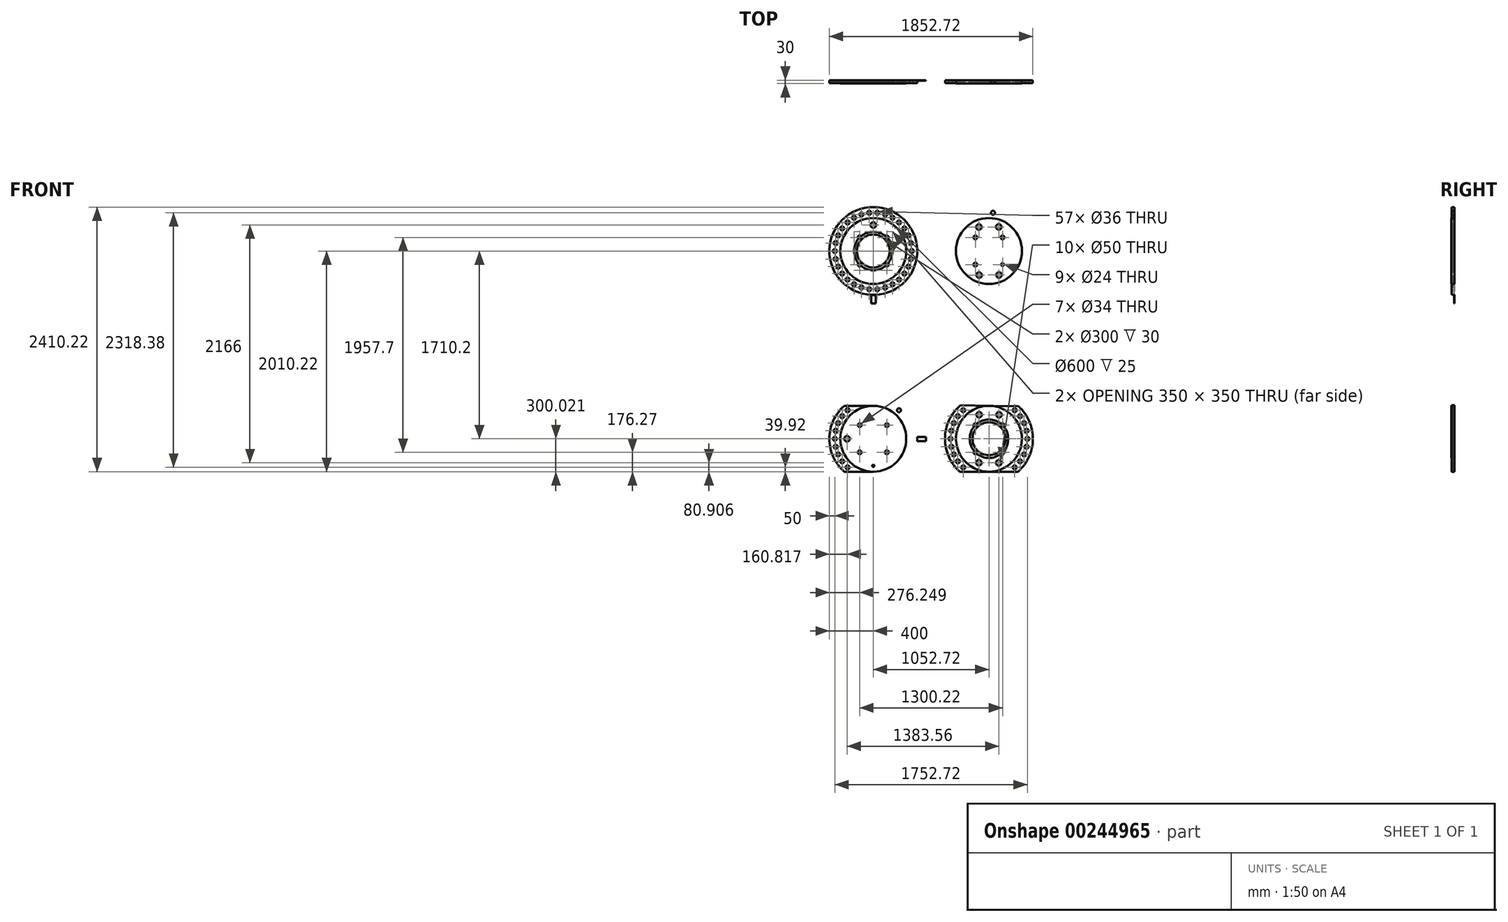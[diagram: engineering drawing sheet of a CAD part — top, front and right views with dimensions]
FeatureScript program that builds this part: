
annotation { "Feature Type Name" : "Feature", "Feature Type Description" : "" }
export const myFeature = defineFeature(function(context is Context, id is Id, definition is map)
    precondition{}
    {
        {
            var Q0;
            Q0=qCreatedBy(makeId("Front.planeOp"),FACE);
            var sketch = newSketch(context, id + "F0", { "sketchPlane" : qUnion([Q0])});
            skCircle(sketch, "E0", {"center": v(0, 0) * mm, "radius": 150 * mm});
            skCircle(sketch, "E1", {"center": v(0, 0) * mm, "radius": 175 * mm});
            skLineSegment(sketch, "E2", {"start": v(-223.66, 0) * mm, "end": v(241.08, 0) * mm, "construction": true});
            skCircle(sketch, "E3", {"center": v(-123.75, 123.74) * mm, "radius": 12 * mm});
            skCircle(sketch, "E4.1.0", {"center": v(-123.74, -123.75) * mm, "radius": 12 * mm});
            skCircle(sketch, "E4.2.0", {"center": v(123.75, -123.74) * mm, "radius": 12 * mm});
            skCircle(sketch, "E4.3.0", {"center": v(123.74, 123.75) * mm, "radius": 12 * mm});
            skLineSegment(sketch, "E5", {"start": v(0, 0) * mm, "end": v(0, 220.77) * mm, "construction": true});
            skCircle(sketch, "E6", {"center": v(-123.75, 123.74) * mm, "radius": 17 * mm});
            skCircle(sketch, "E7", {"center": v(123.74, 123.75) * mm, "radius": 17 * mm});
            skCircle(sketch, "E8", {"center": v(123.75, -123.74) * mm, "radius": 17 * mm});
            skCircle(sketch, "E9", {"center": v(-123.74, -123.75) * mm, "radius": 17 * mm});
            skCircle(sketch, "E10", {"center": v(0, 0) * mm, "radius": 300 * mm});
            skCircle(sketch, "E11", {"center": v(0, 0) * mm, "radius": 350 * mm, "construction": true});
            skCircle(sketch, "E12", {"center": v(0, 0) * mm, "radius": 400 * mm});
            skCircle(sketch, "E13", {"center": v(-350, 0) * mm, "radius": 18 * mm});
            skCircle(sketch, "E14.1.0", {"center": v(-342.35, -72.77) * mm, "radius": 18 * mm});
            skCircle(sketch, "E14.2.0", {"center": v(-319.74, -142.36) * mm, "radius": 18 * mm});
            skCircle(sketch, "E14.3.0", {"center": v(-283.16, -205.72) * mm, "radius": 18 * mm});
            skCircle(sketch, "E14.4.0", {"center": v(-234.2, -260.1) * mm, "radius": 18 * mm});
            skCircle(sketch, "E14.5.0", {"center": v(-175, -303.1) * mm, "radius": 18 * mm});
            skCircle(sketch, "E14.6.0", {"center": v(-108.16, -332.87) * mm, "radius": 18 * mm});
            skCircle(sketch, "E14.7.0", {"center": v(-36.58, -348.08) * mm, "radius": 18 * mm});
            skCircle(sketch, "E14.8.0", {"center": v(36.58, -348.08) * mm, "radius": 18 * mm});
            skCircle(sketch, "E14.9.0", {"center": v(108.16, -332.87) * mm, "radius": 18 * mm});
            skCircle(sketch, "E14.10.0", {"center": v(175, -303.1) * mm, "radius": 18 * mm});
            skCircle(sketch, "E14.11.0", {"center": v(234.2, -260.1) * mm, "radius": 18 * mm});
            skCircle(sketch, "E14.12.0", {"center": v(283.16, -205.72) * mm, "radius": 18 * mm});
            skCircle(sketch, "E14.13.0", {"center": v(319.74, -142.36) * mm, "radius": 18 * mm});
            skCircle(sketch, "E14.14.0", {"center": v(342.35, -72.77) * mm, "radius": 18 * mm});
            skCircle(sketch, "E14.15.0", {"center": v(350, 0) * mm, "radius": 18 * mm});
            skCircle(sketch, "E14.16.0", {"center": v(342.35, 72.77) * mm, "radius": 18 * mm});
            skCircle(sketch, "E14.17.0", {"center": v(319.74, 142.36) * mm, "radius": 18 * mm});
            skCircle(sketch, "E14.18.0", {"center": v(283.16, 205.72) * mm, "radius": 18 * mm});
            skCircle(sketch, "E14.19.0", {"center": v(234.2, 260.1) * mm, "radius": 18 * mm});
            skCircle(sketch, "E14.20.0", {"center": v(175, 303.1) * mm, "radius": 18 * mm});
            skCircle(sketch, "E14.21.0", {"center": v(108.16, 332.87) * mm, "radius": 18 * mm});
            skCircle(sketch, "E14.22.0", {"center": v(36.58, 348.08) * mm, "radius": 18 * mm});
            skCircle(sketch, "E14.23.0", {"center": v(-36.58, 348.08) * mm, "radius": 18 * mm});
            skCircle(sketch, "E14.24.0", {"center": v(-108.16, 332.87) * mm, "radius": 18 * mm});
            skCircle(sketch, "E14.25.0", {"center": v(-175, 303.1) * mm, "radius": 18 * mm});
            skCircle(sketch, "E14.26.0", {"center": v(-234.2, 260.1) * mm, "radius": 18 * mm});
            skCircle(sketch, "E14.27.0", {"center": v(-283.16, 205.72) * mm, "radius": 18 * mm});
            skCircle(sketch, "E14.28.0", {"center": v(-319.74, 142.36) * mm, "radius": 18 * mm});
            skCircle(sketch, "E14.29.0", {"center": v(-342.35, 72.77) * mm, "radius": 18 * mm});
            skLineSegment(sketch, "E15", {"start": v(526.36, 521.4) * mm, "end": v(526.36, -601.38) * mm});
            skPoint(sketch, "E16.center", {"position": v(0, 9.08) * mm});
            skPoint(sketch, "E17.MirrorP", {"position": v(1052.72, 0) * mm});
            skPoint(sketch, "E18.MirrorP", {"position": v(1052.72, 9.08) * mm});
            skCircle(sketch, "E19.MirrorC", {"center": v(928.98, 123.75) * mm, "radius": 12 * mm});
            skCircle(sketch, "E20.MirrorC", {"center": v(1176.47, 123.74) * mm, "radius": 12 * mm});
            skCircle(sketch, "E21.MirrorC", {"center": v(1089.3, 348.08) * mm, "radius": 18 * mm});
            skCircle(sketch, "E22.MirrorC", {"center": v(1335.88, -205.72) * mm, "radius": 18 * mm});
            skCircle(sketch, "E23.MirrorC", {"center": v(769.56, 205.72) * mm, "radius": 18 * mm});
            skCircle(sketch, "E24.MirrorC", {"center": v(1142.22, 219.11) * mm, "radius": 25 * mm});
            skCircle(sketch, "E25.MirrorC", {"center": v(963.22, -219.11) * mm, "radius": 25 * mm});
            skCircle(sketch, "E26.MirrorC", {"center": v(1286.92, -260.1) * mm, "radius": 18 * mm});
            skCircle(sketch, "E27.MirrorC", {"center": v(1395.07, 72.77) * mm, "radius": 18 * mm});
            skCircle(sketch, "E28.MirrorC", {"center": v(961.07, 218.22) * mm, "radius": 25 * mm});
            skCircle(sketch, "E29.MirrorC", {"center": v(818.53, 260.1) * mm, "radius": 18 * mm});
            skCircle(sketch, "E30.MirrorC", {"center": v(928.97, -123.74) * mm, "radius": 17 * mm});
            skCircle(sketch, "E31.MirrorC", {"center": v(928.98, 123.75) * mm, "radius": 17 * mm});
            skCircle(sketch, "E32.MirrorC", {"center": v(1176.47, 123.74) * mm, "radius": 17 * mm});
            skLineSegment(sketch, "E33.MirrorCS", {"start": v(1276.38, 0) * mm, "end": v(811.64, 0) * mm, "construction": true});
            skCircle(sketch, "E34.MirrorC", {"center": v(1052.72, 0) * mm, "radius": 175 * mm});
            skCircle(sketch, "E35.MirrorC", {"center": v(1052.72, 0) * mm, "radius": 400 * mm});
            skCircle(sketch, "E36.MirrorC", {"center": v(1372.46, -142.36) * mm, "radius": 18 * mm});
            skCircle(sketch, "E37.MirrorC", {"center": v(710.37, 72.77) * mm, "radius": 18 * mm});
            skCircle(sketch, "E38.MirrorC", {"center": v(702.72, 0) * mm, "radius": 18 * mm});
            skCircle(sketch, "E39.MirrorC", {"center": v(1052.72, 0) * mm, "radius": 236.69 * mm, "construction": true});
            skCircle(sketch, "E40.MirrorC", {"center": v(1016.14, 348.08) * mm, "radius": 18 * mm});
            skCircle(sketch, "E41.MirrorC", {"center": v(1227.72, 303.1) * mm, "radius": 18 * mm});
            skCircle(sketch, "E42.MirrorC", {"center": v(732.98, -142.36) * mm, "radius": 18 * mm});
            skCircle(sketch, "E43.MirrorC", {"center": v(818.53, -260.1) * mm, "radius": 18 * mm});
            skCircle(sketch, "E44.MirrorC", {"center": v(1402.72, 0) * mm, "radius": 18 * mm});
            skCircle(sketch, "E45.MirrorC", {"center": v(1395.07, -72.77) * mm, "radius": 18 * mm});
            skCircle(sketch, "E46.MirrorC", {"center": v(1052.72, 0) * mm, "radius": 150 * mm});
            skCircle(sketch, "E47.MirrorC", {"center": v(1286.92, 260.1) * mm, "radius": 18 * mm});
            skCircle(sketch, "E48.MirrorC", {"center": v(1144.37, -218.22) * mm, "radius": 25 * mm});
            skCircle(sketch, "E49.MirrorC", {"center": v(877.72, 303.1) * mm, "radius": 18 * mm});
            skCircle(sketch, "E50.MirrorC", {"center": v(732.98, 142.36) * mm, "radius": 18 * mm});
            skLineSegment(sketch, "E51.MirrorCS", {"start": v(1052.72, 0) * mm, "end": v(1052.72, 220.77) * mm, "construction": true});
            skCircle(sketch, "E52.MirrorC", {"center": v(1052.72, 0) * mm, "radius": 350 * mm, "construction": true});
            skCircle(sketch, "E53.MirrorC", {"center": v(1335.88, 205.72) * mm, "radius": 18 * mm});
            skCircle(sketch, "E54.MirrorC", {"center": v(1160.88, 332.87) * mm, "radius": 18 * mm});
            skCircle(sketch, "E55.MirrorC", {"center": v(1372.46, 142.36) * mm, "radius": 18 * mm});
            skCircle(sketch, "E56.MirrorC", {"center": v(944.56, 332.87) * mm, "radius": 18 * mm});
            skCircle(sketch, "E57.MirrorC", {"center": v(1176.46, -123.75) * mm, "radius": 12 * mm});
            skCircle(sketch, "E58.MirrorC", {"center": v(769.56, -205.72) * mm, "radius": 18 * mm});
            skCircle(sketch, "E59.MirrorC", {"center": v(1052.72, 0) * mm, "radius": 300 * mm});
            skCircle(sketch, "E60.MirrorC", {"center": v(710.37, -72.77) * mm, "radius": 18 * mm});
            skCircle(sketch, "E61.MirrorC", {"center": v(928.97, -123.74) * mm, "radius": 12 * mm});
            skCircle(sketch, "E62.MirrorC", {"center": v(1176.46, -123.75) * mm, "radius": 17 * mm});
            skLineSegment(sketch, "E63", {"start": v(-563.71, -855.1) * mm, "end": v(1645.53, -855.1) * mm});
            skCircle(sketch, "E64.MirrorC", {"center": v(1176.47, -1833.94) * mm, "radius": 17 * mm});
            skCircle(sketch, "E65.MirrorC", {"center": v(928.97, -1586.46) * mm, "radius": 17 * mm});
            skCircle(sketch, "E66.MirrorC", {"center": v(-123.75, -1833.94) * mm, "radius": 12 * mm});
            skPoint(sketch, "E67.MirrorP", {"position": v(1052.72, -1710.2) * mm});
            skPoint(sketch, "E68.MirrorP", {"position": v(0, -1719.28) * mm});
            skCircle(sketch, "E69.MirrorC", {"center": v(1176.46, -1586.45) * mm, "radius": 17 * mm});
            skCircle(sketch, "E70.MirrorC", {"center": v(-123.74, -1586.45) * mm, "radius": 17 * mm});
            skCircle(sketch, "E71.MirrorC", {"center": v(123.75, -1586.46) * mm, "radius": 12 * mm});
            skCircle(sketch, "E72.MirrorC", {"center": v(-123.74, -1586.45) * mm, "radius": 12 * mm});
            skCircle(sketch, "E73.MirrorC", {"center": v(-123.75, -1833.94) * mm, "radius": 17 * mm});
            skCircle(sketch, "E74.MirrorC", {"center": v(928.97, -1586.46) * mm, "radius": 12 * mm});
            skCircle(sketch, "E75.MirrorC", {"center": v(928.98, -1833.95) * mm, "radius": 17 * mm});
            skCircle(sketch, "E76.MirrorC", {"center": v(123.74, -1833.95) * mm, "radius": 12 * mm});
            skCircle(sketch, "E77.MirrorC", {"center": v(928.98, -1833.95) * mm, "radius": 12 * mm});
            skCircle(sketch, "E78.MirrorC", {"center": v(1176.47, -1833.94) * mm, "radius": 12 * mm});
            skCircle(sketch, "E79.MirrorC", {"center": v(1176.46, -1586.45) * mm, "radius": 12 * mm});
            skCircle(sketch, "E80.MirrorC", {"center": v(-319.74, -1567.84) * mm, "radius": 18 * mm});
            skCircle(sketch, "E81.MirrorC", {"center": v(-350, -1710.2) * mm, "radius": 18 * mm});
            skCircle(sketch, "E82.MirrorC", {"center": v(-342.35, -1637.43) * mm, "radius": 18 * mm});
            skCircle(sketch, "E83.MirrorC", {"center": v(-342.35, -1782.97) * mm, "radius": 18 * mm});
            skCircle(sketch, "E84.MirrorC", {"center": v(-319.74, -1852.56) * mm, "radius": 18 * mm});
            skPoint(sketch, "E85.MirrorP", {"position": v(0, -1710.2) * mm});
            skPoint(sketch, "E86.MirrorP", {"position": v(1052.72, -1719.28) * mm});
            skCircle(sketch, "E87.MirrorC", {"center": v(710.37, -1637.43) * mm, "radius": 18 * mm});
            skCircle(sketch, "E88.MirrorC", {"center": v(-283.16, -1915.92) * mm, "radius": 18 * mm});
            skCircle(sketch, "E89.MirrorC", {"center": v(234.2, -1450.1) * mm, "radius": 18 * mm});
            skCircle(sketch, "E90.MirrorC", {"center": v(1052.72, -1710.2) * mm, "radius": 236.69 * mm, "construction": true});
            skCircle(sketch, "E91.MirrorC", {"center": v(-234.2, -1450.1) * mm, "radius": 18 * mm});
            skCircle(sketch, "E92.MirrorC", {"center": v(1052.72, -1710.2) * mm, "radius": 150 * mm});
            skLineSegment(sketch, "E93.MirrorCS", {"start": v(1276.38, -1710.2) * mm, "end": v(811.64, -1710.2) * mm, "construction": true});
            skCircle(sketch, "E94.MirrorC", {"center": v(963.22, -1491.08) * mm, "radius": 25 * mm});
            skCircle(sketch, "E95.MirrorC", {"center": v(-234.2, -1970.3) * mm, "radius": 18 * mm});
            skCircle(sketch, "E96.MirrorC", {"center": v(-283.16, -1504.47) * mm, "radius": 18 * mm});
            skCircle(sketch, "E97.MirrorC", {"center": v(702.72, -1710.2) * mm, "radius": 18 * mm});
            skCircle(sketch, "E98.MirrorC", {"center": v(0, -1710.2) * mm, "radius": 300 * mm});
            skCircle(sketch, "E99.MirrorC", {"center": v(1052.72, -1710.2) * mm, "radius": 350 * mm, "construction": true});
            skCircle(sketch, "E100.MirrorC", {"center": v(123.74, -1833.95) * mm, "radius": 17 * mm});
            skCircle(sketch, "E101.MirrorC", {"center": v(0, -1710.2) * mm, "radius": 400 * mm});
            skCircle(sketch, "E102.MirrorC", {"center": v(1395.07, -1637.43) * mm, "radius": 18 * mm});
            skCircle(sketch, "E103.MirrorC", {"center": v(283.16, -1915.92) * mm, "radius": 18 * mm});
            skCircle(sketch, "E104.MirrorC", {"center": v(319.74, -1852.56) * mm, "radius": 18 * mm});
            skCircle(sketch, "E105.MirrorC", {"center": v(818.53, -1970.3) * mm, "radius": 18 * mm});
            skCircle(sketch, "E106.MirrorC", {"center": v(1052.72, -1710.2) * mm, "radius": 400 * mm});
            skCircle(sketch, "E107.MirrorC", {"center": v(732.98, -1567.84) * mm, "radius": 18 * mm});
            skLineSegment(sketch, "E108.MirrorCS", {"start": v(-223.66, -1710.2) * mm, "end": v(241.08, -1710.2) * mm, "construction": true});
            skCircle(sketch, "E109.MirrorC", {"center": v(769.56, -1504.47) * mm, "radius": 18 * mm});
            skCircle(sketch, "E110.MirrorC", {"center": v(0, -1710.2) * mm, "radius": 175 * mm});
            skCircle(sketch, "E111.MirrorC", {"center": v(769.56, -1915.92) * mm, "radius": 18 * mm});
            skCircle(sketch, "E112.MirrorC", {"center": v(350, -1710.2) * mm, "radius": 18 * mm});
            skCircle(sketch, "E113.MirrorC", {"center": v(961.07, -1928.42) * mm, "radius": 25 * mm});
            skCircle(sketch, "E114.MirrorC", {"center": v(1052.72, -1710.2) * mm, "radius": 175 * mm});
            skCircle(sketch, "E115.MirrorC", {"center": v(1144.37, -1491.98) * mm, "radius": 25 * mm});
            skCircle(sketch, "E116.MirrorC", {"center": v(319.74, -1567.84) * mm, "radius": 18 * mm});
            skCircle(sketch, "E117.MirrorC", {"center": v(1335.88, -1504.47) * mm, "radius": 18 * mm});
            skCircle(sketch, "E118.MirrorC", {"center": v(1372.46, -1852.56) * mm, "radius": 18 * mm});
            skCircle(sketch, "E119.MirrorC", {"center": v(342.35, -1637.43) * mm, "radius": 18 * mm});
            skCircle(sketch, "E120.MirrorC", {"center": v(123.75, -1586.46) * mm, "radius": 17 * mm});
            skCircle(sketch, "E121.MirrorC", {"center": v(1335.88, -1915.92) * mm, "radius": 18 * mm});
            skCircle(sketch, "E122.MirrorC", {"center": v(283.16, -1504.47) * mm, "radius": 18 * mm});
            skCircle(sketch, "E123.MirrorC", {"center": v(1286.92, -1450.1) * mm, "radius": 18 * mm});
            skCircle(sketch, "E124.MirrorC", {"center": v(1052.72, -1710.2) * mm, "radius": 300 * mm});
            skCircle(sketch, "E125.MirrorC", {"center": v(0, -1710.2) * mm, "radius": 350 * mm, "construction": true});
            skCircle(sketch, "E126.MirrorC", {"center": v(234.2, -1970.3) * mm, "radius": 18 * mm});
            skCircle(sketch, "E127.MirrorC", {"center": v(342.35, -1782.97) * mm, "radius": 18 * mm});
            skCircle(sketch, "E128.MirrorC", {"center": v(1372.46, -1567.84) * mm, "radius": 18 * mm});
            skCircle(sketch, "E129.MirrorC", {"center": v(732.98, -1852.56) * mm, "radius": 18 * mm});
            skCircle(sketch, "E130.MirrorC", {"center": v(1286.92, -1970.3) * mm, "radius": 18 * mm});
            skCircle(sketch, "E131.MirrorC", {"center": v(0, -1710.2) * mm, "radius": 150 * mm});
            skCircle(sketch, "E132.MirrorC", {"center": v(1395.07, -1782.97) * mm, "radius": 18 * mm});
            skLineSegment(sketch, "E133.MirrorCS", {"start": v(526.36, -2231.6) * mm, "end": v(526.36, -1108.82) * mm});
            skCircle(sketch, "E134.MirrorC", {"center": v(1402.72, -1710.2) * mm, "radius": 18 * mm});
            skLineSegment(sketch, "E135.MirrorCS", {"start": v(0, -1710.2) * mm, "end": v(0, -1930.97) * mm, "construction": true});
            skLineSegment(sketch, "E136.MirrorCS", {"start": v(1052.72, -1710.2) * mm, "end": v(1052.72, -1930.97) * mm, "construction": true});
            skCircle(sketch, "E137.MirrorC", {"center": v(710.37, -1782.97) * mm, "radius": 18 * mm});
            skCircle(sketch, "E138.MirrorC", {"center": v(818.53, -1450.1) * mm, "radius": 18 * mm});
            skCircle(sketch, "E139.MirrorC", {"center": v(1142.22, -1929.31) * mm, "radius": 25 * mm});
            skLineSegment(sketch, "E140.bottom", {"start": v(-18.4, -399.58) * mm, "end": v(21.24, -399.58) * mm});
            skLineSegment(sketch, "E140.top", {"start": v(-18.4, -477.62) * mm, "end": v(21.24, -477.62) * mm});
            skLineSegment(sketch, "E140.left", {"start": v(-18.4, -399.58) * mm, "end": v(-18.4, -477.62) * mm});
            skLineSegment(sketch, "E140.right", {"start": v(21.24, -399.58) * mm, "end": v(21.24, -477.62) * mm});
            skLineSegment(sketch, "E141", {"start": v(0, 0) * mm, "end": v(0, 258.46) * mm, "construction": true});
            skCircle(sketch, "E142", {"center": v(0, 236.69) * mm, "radius": 25 * mm});
            skLineSegment(sketch, "E143", {"start": v(816.8, -323.02) * mm, "end": v(1288.65, -323.02) * mm});
            skLineSegment(sketch, "E144", {"start": v(794.92, -305.84) * mm, "end": v(1306.54, -309.15) * mm});
            skLineSegment(sketch, "E145", {"start": v(1057.02, -2010.17) * mm, "end": v(688.2, -2010.17) * mm});
            skLineSegment(sketch, "E146", {"start": v(688.2, -2010.17) * mm, "end": v(1404.33, -2010.23) * mm});
            skLineSegment(sketch, "E147", {"start": v(1057.3, -1410.23) * mm, "end": v(1057.3, -1410.23) * mm});
            skLineSegment(sketch, "E148", {"start": v(1057.3, -1410.23) * mm, "end": v(1440.91, -1416.08) * mm});
            skLineSegment(sketch, "E149", {"start": v(1440.91, -1416.08) * mm, "end": v(685.36, -1404.57) * mm});
            skLineSegment(sketch, "E150", {"start": v(0, -1719.28) * mm, "end": v(0, -1993.4) * mm, "construction": true});
            skLineSegment(sketch, "E151.bottom", {"start": v(399.67, -1693.9) * mm, "end": v(480.07, -1693.9) * mm});
            skLineSegment(sketch, "E151.top", {"start": v(399.67, -1733.02) * mm, "end": v(480.07, -1733.02) * mm});
            skLineSegment(sketch, "E151.left", {"start": v(399.67, -1693.9) * mm, "end": v(399.67, -1733.02) * mm});
            skLineSegment(sketch, "E151.right", {"start": v(480.07, -1693.9) * mm, "end": v(480.07, -1733.02) * mm});
            skLineSegment(sketch, "E152", {"start": v(0, -1410.2) * mm, "end": v(-512.36, -1410.2) * mm});
            skLineSegment(sketch, "E153", {"start": v(-512.36, -1410.2) * mm, "end": v(403.74, -1410.2) * mm});
            skLineSegment(sketch, "E154", {"start": v(0, -2010.2) * mm, "end": v(-415.08, -2010.2) * mm});
            skLineSegment(sketch, "E155", {"start": v(-415.08, -2010.2) * mm, "end": v(414.55, -2010.2) * mm});
            skCircle(sketch, "E156", {"center": v(-239.18, -1710.2) * mm, "radius": 25 * mm});
            skCircle(sketch, "E157", {"center": v(0, -1955.83) * mm, "radius": 10 * mm});
            skSolve(sketch);
        }
        {
            var Q0;
            Q0=makeQuery(id+"F0.imprint","IMPRINT",FACE,{"disambiguationData":[TD([[makeQuery(id+"F0.imprint","IMPRINT",EDGE,{"derivedFrom":sQuery(id+"F0.wireOp",EDGE,"E80.MirrorC")}),1.0]])]});
            var Q1;
            Q1=makeQuery(id+"F0.imprint","IMPRINT",FACE,{"disambiguationData":[TD([[makeQuery(id+"F0.imprint","IMPRINT",EDGE,{"derivedFrom":sQuery(id+"F0.wireOp",EDGE,"E87.MirrorC")}),-1.0]])]});
            var Q2;
            Q2=makeQuery(id+"F0.imprint","IMPRINT",FACE,{"disambiguationData":[TD([[makeQuery(id+"F0.imprint","IMPRINT",EDGE,{"derivedFrom":sQuery(id+"F0.wireOp",EDGE,"E102.MirrorC")}),-1.0]])]});
            var Q3;
            Q3=makeQuery(id+"F0.imprint","IMPRINT",FACE,{"disambiguationData":[TD([[makeQuery(id+"F0.imprint","IMPRINT",EDGE,{"derivedFrom":sQuery(id+"F0.wireOp",EDGE,"E21.MirrorC")}),1.0]])]});
            var Q4;
            Q4=makeQuery(id+"F0.imprint","IMPRINT",FACE,{"disambiguationData":[TD([[makeQuery(id+"F0.imprint","IMPRINT",EDGE,{"derivedFrom":sQuery(id+"F0.wireOp",EDGE,"E10")}),-1.0]])]});
            var Q5;
            Q5=makeQuery(id+"F0.imprint","IMPRINT",FACE,{"disambiguationData":[TD([[makeQuery(id+"F0.imprint","IMPRINT",EDGE,{"derivedFrom":sQuery(id+"F0.wireOp",EDGE,"E89.MirrorC")}),1.0]])]});
            extrude(context, id + "F1", {"entities" : qUnion([Q0, Q1, Q2, Q3, Q4, Q5]), "depth" : 25 * mm});
        }
        {
            var Q0;
            Q0=makeQuery(id+"F0.imprint","IMPRINT",FACE,{"disambiguationData":[TD([[makeQuery(id+"F0.imprint","IMPRINT",EDGE,{"derivedFrom":sQuery(id+"F0.wireOp",EDGE,"E10")}),1.0]])]});
            var Q1;
            Q1=makeQuery(id+"F0.imprint","IMPRINT",FACE,{"disambiguationData":[TD([[makeQuery(id+"F0.imprint","IMPRINT",EDGE,{"derivedFrom":sQuery(id+"F0.wireOp",EDGE,"E24.MirrorC")}),1.0]])]});
            var Q2;
            Q2=makeQuery(id+"F0.imprint","IMPRINT",FACE,{"disambiguationData":[TD([[makeQuery(id+"F0.imprint","IMPRINT",EDGE,{"derivedFrom":sQuery(id+"F0.wireOp",EDGE,"E98.MirrorC")}),-1.0]])]});
            var Q3;
            Q3=makeQuery(id+"F0.imprint","IMPRINT",FACE,{"disambiguationData":[TD([[makeQuery(id+"F0.imprint","IMPRINT",EDGE,{"derivedFrom":sQuery(id+"F0.wireOp",EDGE,"E94.MirrorC")}),-1.0]])]});
            extrude(context, id + "F2", {"entities" : qUnion([Q0, Q1, Q2, Q3]), "depth" : 10 * mm});
        }
        {
            var Q0;
            Q0=makeQuery(id+"F0.imprint","IMPRINT",FACE,{"disambiguationData":[TD([[makeQuery(id+"F0.imprint","IMPRINT",EDGE,{"derivedFrom":sQuery(id+"F0.wireOp",EDGE,"E131.MirrorC")}),1.0]])]});
            var Q1;
            {var subQ0=sQuery(id+"F0.wireOp",EDGE,"E110.MirrorC");var subQ1=sQuery(id+"F0.wireOp",EDGE,"E71.MirrorC");var subQ2=makeQuery(id+"F0.imprint","INTERSECT",VERTEX,{"disambiguationData":[OD(0.0)],"derivedFrom":[subQ1,subQ0]});Q1=makeQuery(id+"F0.imprint","IMPRINT",FACE,{"disambiguationData":[TD([[makeQuery(id+"F0.imprint","IMPRINT",EDGE,{"disambiguationData":[TD([[subQ2,1.0]])],"derivedFrom":subQ1}),1.0]])]});}
            var Q2;
            {var subQ0=sQuery(id+"F0.wireOp",EDGE,"E110.MirrorC");var subQ1=sQuery(id+"F0.wireOp",EDGE,"E71.MirrorC");var subQ2=makeQuery(id+"F0.imprint","INTERSECT",VERTEX,{"disambiguationData":[OD(0.0)],"derivedFrom":[subQ1,subQ0]});Q2=makeQuery(id+"F0.imprint","IMPRINT",FACE,{"disambiguationData":[TD([[makeQuery(id+"F0.imprint","IMPRINT",EDGE,{"disambiguationData":[TD([[subQ2,-1.0]])],"derivedFrom":subQ1}),1.0]])]});}
            var Q3;
            {var subQ0=sQuery(id+"F0.wireOp",EDGE,"E110.MirrorC");var subQ1=sQuery(id+"F0.wireOp",EDGE,"E70.MirrorC");var subQ2=makeQuery(id+"F0.imprint","INTERSECT",VERTEX,{"disambiguationData":[OD(0.0)],"derivedFrom":[subQ1,subQ0]});Q3=makeQuery(id+"F0.imprint","IMPRINT",FACE,{"disambiguationData":[TD([[makeQuery(id+"F0.imprint","IMPRINT",EDGE,{"disambiguationData":[TD([[subQ2,1.0]])],"derivedFrom":subQ1}),-1.0]])]});}
            var Q4;
            {var subQ0=sQuery(id+"F0.wireOp",EDGE,"E110.MirrorC");var subQ1=sQuery(id+"F0.wireOp",EDGE,"E70.MirrorC");var subQ2=makeQuery(id+"F0.imprint","INTERSECT",VERTEX,{"disambiguationData":[OD(0.0)],"derivedFrom":[subQ1,subQ0]});Q4=makeQuery(id+"F0.imprint","IMPRINT",FACE,{"disambiguationData":[TD([[makeQuery(id+"F0.imprint","IMPRINT",EDGE,{"disambiguationData":[TD([[subQ2,-1.0]])],"derivedFrom":subQ1}),-1.0]])]});}
            var Q5;
            {var subQ0=sQuery(id+"F0.wireOp",EDGE,"E110.MirrorC");var subQ1=sQuery(id+"F0.wireOp",EDGE,"E66.MirrorC");var subQ2=makeQuery(id+"F0.imprint","INTERSECT",VERTEX,{"disambiguationData":[OD(0.0)],"derivedFrom":[subQ1,subQ0]});Q5=makeQuery(id+"F0.imprint","IMPRINT",FACE,{"disambiguationData":[TD([[makeQuery(id+"F0.imprint","IMPRINT",EDGE,{"disambiguationData":[TD([[subQ2,1.0]])],"derivedFrom":subQ1}),1.0]])]});}
            var Q6;
            {var subQ0=sQuery(id+"F0.wireOp",EDGE,"E110.MirrorC");var subQ1=sQuery(id+"F0.wireOp",EDGE,"E66.MirrorC");var subQ2=makeQuery(id+"F0.imprint","INTERSECT",VERTEX,{"disambiguationData":[OD(0.0)],"derivedFrom":[subQ1,subQ0]});Q6=makeQuery(id+"F0.imprint","IMPRINT",FACE,{"disambiguationData":[TD([[makeQuery(id+"F0.imprint","IMPRINT",EDGE,{"disambiguationData":[TD([[subQ2,-1.0]])],"derivedFrom":subQ1}),1.0]])]});}
            var Q7;
            {var subQ0=sQuery(id+"F0.wireOp",EDGE,"E110.MirrorC");var subQ1=sQuery(id+"F0.wireOp",EDGE,"E76.MirrorC");var subQ2=makeQuery(id+"F0.imprint","INTERSECT",VERTEX,{"disambiguationData":[OD(0.0)],"derivedFrom":[subQ1,subQ0]});Q7=makeQuery(id+"F0.imprint","IMPRINT",FACE,{"disambiguationData":[TD([[makeQuery(id+"F0.imprint","IMPRINT",EDGE,{"disambiguationData":[TD([[subQ2,1.0]])],"derivedFrom":subQ1}),1.0]])]});}
            var Q8;
            {var subQ0=sQuery(id+"F0.wireOp",EDGE,"E110.MirrorC");var subQ1=sQuery(id+"F0.wireOp",EDGE,"E76.MirrorC");var subQ2=makeQuery(id+"F0.imprint","INTERSECT",VERTEX,{"disambiguationData":[OD(0.0)],"derivedFrom":[subQ1,subQ0]});Q8=makeQuery(id+"F0.imprint","IMPRINT",FACE,{"disambiguationData":[TD([[makeQuery(id+"F0.imprint","IMPRINT",EDGE,{"disambiguationData":[TD([[subQ2,-1.0]])],"derivedFrom":subQ1}),1.0]])]});}
            var Q9;
            Q9=makeQuery(id+"F0.imprint","IMPRINT",FACE,{"disambiguationData":[TD([[makeQuery(id+"F0.imprint","IMPRINT",EDGE,{"derivedFrom":sQuery(id+"F0.wireOp",EDGE,"E92.MirrorC")}),-1.0]])]});
            var Q10;
            {var subQ0=sQuery(id+"F0.wireOp",EDGE,"E114.MirrorC");var subQ1=sQuery(id+"F0.wireOp",EDGE,"E75.MirrorC");var subQ2=makeQuery(id+"F0.imprint","INTERSECT",VERTEX,{"disambiguationData":[OD(0.0)],"derivedFrom":[subQ1,subQ0]});Q10=makeQuery(id+"F0.imprint","IMPRINT",FACE,{"disambiguationData":[TD([[makeQuery(id+"F0.imprint","IMPRINT",EDGE,{"disambiguationData":[TD([[subQ2,1.0]])],"derivedFrom":subQ1}),1.0]])]});}
            var Q11;
            {var subQ0=sQuery(id+"F0.wireOp",EDGE,"E114.MirrorC");var subQ1=sQuery(id+"F0.wireOp",EDGE,"E75.MirrorC");var subQ2=makeQuery(id+"F0.imprint","INTERSECT",VERTEX,{"disambiguationData":[OD(0.0)],"derivedFrom":[subQ1,subQ0]});Q11=makeQuery(id+"F0.imprint","IMPRINT",FACE,{"disambiguationData":[TD([[makeQuery(id+"F0.imprint","IMPRINT",EDGE,{"disambiguationData":[TD([[subQ2,-1.0]])],"derivedFrom":subQ1}),1.0]])]});}
            var Q12;
            {var subQ0=sQuery(id+"F0.wireOp",EDGE,"E114.MirrorC");var subQ1=sQuery(id+"F0.wireOp",EDGE,"E64.MirrorC");var subQ2=makeQuery(id+"F0.imprint","INTERSECT",VERTEX,{"disambiguationData":[OD(0.0)],"derivedFrom":[subQ1,subQ0]});Q12=makeQuery(id+"F0.imprint","IMPRINT",FACE,{"disambiguationData":[TD([[makeQuery(id+"F0.imprint","IMPRINT",EDGE,{"disambiguationData":[TD([[subQ2,1.0]])],"derivedFrom":subQ1}),1.0]])]});}
            var Q13;
            {var subQ0=sQuery(id+"F0.wireOp",EDGE,"E114.MirrorC");var subQ1=sQuery(id+"F0.wireOp",EDGE,"E64.MirrorC");var subQ2=makeQuery(id+"F0.imprint","INTERSECT",VERTEX,{"disambiguationData":[OD(0.0)],"derivedFrom":[subQ1,subQ0]});Q13=makeQuery(id+"F0.imprint","IMPRINT",FACE,{"disambiguationData":[TD([[makeQuery(id+"F0.imprint","IMPRINT",EDGE,{"disambiguationData":[TD([[subQ2,-1.0]])],"derivedFrom":subQ1}),1.0]])]});}
            var Q14;
            {var subQ0=sQuery(id+"F0.wireOp",EDGE,"E114.MirrorC");var subQ1=sQuery(id+"F0.wireOp",EDGE,"E69.MirrorC");var subQ2=makeQuery(id+"F0.imprint","INTERSECT",VERTEX,{"disambiguationData":[OD(0.0)],"derivedFrom":[subQ1,subQ0]});Q14=makeQuery(id+"F0.imprint","IMPRINT",FACE,{"disambiguationData":[TD([[makeQuery(id+"F0.imprint","IMPRINT",EDGE,{"disambiguationData":[TD([[subQ2,1.0]])],"derivedFrom":subQ1}),1.0]])]});}
            var Q15;
            {var subQ0=sQuery(id+"F0.wireOp",EDGE,"E114.MirrorC");var subQ1=sQuery(id+"F0.wireOp",EDGE,"E69.MirrorC");var subQ2=makeQuery(id+"F0.imprint","INTERSECT",VERTEX,{"disambiguationData":[OD(0.0)],"derivedFrom":[subQ1,subQ0]});Q15=makeQuery(id+"F0.imprint","IMPRINT",FACE,{"disambiguationData":[TD([[makeQuery(id+"F0.imprint","IMPRINT",EDGE,{"disambiguationData":[TD([[subQ2,-1.0]])],"derivedFrom":subQ1}),1.0]])]});}
            var Q16;
            {var subQ0=sQuery(id+"F0.wireOp",EDGE,"E114.MirrorC");var subQ1=sQuery(id+"F0.wireOp",EDGE,"E65.MirrorC");var subQ2=makeQuery(id+"F0.imprint","INTERSECT",VERTEX,{"disambiguationData":[OD(0.0)],"derivedFrom":[subQ1,subQ0]});Q16=makeQuery(id+"F0.imprint","IMPRINT",FACE,{"disambiguationData":[TD([[makeQuery(id+"F0.imprint","IMPRINT",EDGE,{"disambiguationData":[TD([[subQ2,1.0]])],"derivedFrom":subQ1}),1.0]])]});}
            var Q17;
            {var subQ0=sQuery(id+"F0.wireOp",EDGE,"E114.MirrorC");var subQ1=sQuery(id+"F0.wireOp",EDGE,"E65.MirrorC");var subQ2=makeQuery(id+"F0.imprint","INTERSECT",VERTEX,{"disambiguationData":[OD(0.0)],"derivedFrom":[subQ1,subQ0]});Q17=makeQuery(id+"F0.imprint","IMPRINT",FACE,{"disambiguationData":[TD([[makeQuery(id+"F0.imprint","IMPRINT",EDGE,{"disambiguationData":[TD([[subQ2,-1.0]])],"derivedFrom":subQ1}),1.0]])]});}
            var Q18;
            Q18=makeQuery(id+"F0.imprint","IMPRINT",FACE,{"disambiguationData":[TD([[makeQuery(id+"F0.imprint","IMPRINT",EDGE,{"derivedFrom":sQuery(id+"F0.wireOp",EDGE,"E46.MirrorC")}),1.0]])]});
            var Q19;
            {var subQ0=sQuery(id+"F0.wireOp",EDGE,"E62.MirrorC");var subQ1=sQuery(id+"F0.wireOp",EDGE,"E34.MirrorC");var subQ2=makeQuery(id+"F0.imprint","INTERSECT",VERTEX,{"disambiguationData":[OD(0.0)],"derivedFrom":[subQ1,subQ0]});Q19=makeQuery(id+"F0.imprint","IMPRINT",FACE,{"disambiguationData":[TD([[makeQuery(id+"F0.imprint","IMPRINT",EDGE,{"disambiguationData":[TD([[subQ2,-1.0]])],"derivedFrom":subQ1}),1.0]])]});}
            var Q20;
            {var subQ0=sQuery(id+"F0.wireOp",EDGE,"E62.MirrorC");var subQ1=sQuery(id+"F0.wireOp",EDGE,"E34.MirrorC");var subQ2=makeQuery(id+"F0.imprint","INTERSECT",VERTEX,{"disambiguationData":[OD(0.0)],"derivedFrom":[subQ1,subQ0]});Q20=makeQuery(id+"F0.imprint","IMPRINT",FACE,{"disambiguationData":[TD([[makeQuery(id+"F0.imprint","IMPRINT",EDGE,{"disambiguationData":[TD([[subQ2,-1.0]])],"derivedFrom":subQ1}),-1.0]])]});}
            var Q21;
            {var subQ0=sQuery(id+"F0.wireOp",EDGE,"E34.MirrorC");var subQ1=sQuery(id+"F0.wireOp",EDGE,"E30.MirrorC");var subQ2=makeQuery(id+"F0.imprint","INTERSECT",VERTEX,{"disambiguationData":[OD(0.0)],"derivedFrom":[subQ1,subQ0]});Q21=makeQuery(id+"F0.imprint","IMPRINT",FACE,{"disambiguationData":[TD([[makeQuery(id+"F0.imprint","IMPRINT",EDGE,{"disambiguationData":[TD([[subQ2,1.0]])],"derivedFrom":subQ1}),-1.0]])]});}
            var Q22;
            {var subQ0=sQuery(id+"F0.wireOp",EDGE,"E34.MirrorC");var subQ1=sQuery(id+"F0.wireOp",EDGE,"E30.MirrorC");var subQ2=makeQuery(id+"F0.imprint","INTERSECT",VERTEX,{"disambiguationData":[OD(0.0)],"derivedFrom":[subQ1,subQ0]});Q22=makeQuery(id+"F0.imprint","IMPRINT",FACE,{"disambiguationData":[TD([[makeQuery(id+"F0.imprint","IMPRINT",EDGE,{"disambiguationData":[TD([[subQ2,-1.0]])],"derivedFrom":subQ1}),-1.0]])]});}
            var Q23;
            {var subQ0=sQuery(id+"F0.wireOp",EDGE,"E34.MirrorC");var subQ1=sQuery(id+"F0.wireOp",EDGE,"E19.MirrorC");var subQ2=makeQuery(id+"F0.imprint","INTERSECT",VERTEX,{"disambiguationData":[OD(0.0)],"derivedFrom":[subQ1,subQ0]});Q23=makeQuery(id+"F0.imprint","IMPRINT",FACE,{"disambiguationData":[TD([[makeQuery(id+"F0.imprint","IMPRINT",EDGE,{"disambiguationData":[TD([[subQ2,1.0]])],"derivedFrom":subQ1}),1.0]])]});}
            var Q24;
            {var subQ0=sQuery(id+"F0.wireOp",EDGE,"E34.MirrorC");var subQ1=sQuery(id+"F0.wireOp",EDGE,"E19.MirrorC");var subQ2=makeQuery(id+"F0.imprint","INTERSECT",VERTEX,{"disambiguationData":[OD(0.0)],"derivedFrom":[subQ1,subQ0]});Q24=makeQuery(id+"F0.imprint","IMPRINT",FACE,{"disambiguationData":[TD([[makeQuery(id+"F0.imprint","IMPRINT",EDGE,{"disambiguationData":[TD([[subQ2,-1.0]])],"derivedFrom":subQ1}),1.0]])]});}
            var Q25;
            {var subQ0=sQuery(id+"F0.wireOp",EDGE,"E34.MirrorC");var subQ1=sQuery(id+"F0.wireOp",EDGE,"E20.MirrorC");var subQ2=makeQuery(id+"F0.imprint","INTERSECT",VERTEX,{"disambiguationData":[OD(0.0)],"derivedFrom":[subQ1,subQ0]});Q25=makeQuery(id+"F0.imprint","IMPRINT",FACE,{"disambiguationData":[TD([[makeQuery(id+"F0.imprint","IMPRINT",EDGE,{"disambiguationData":[TD([[subQ2,1.0]])],"derivedFrom":subQ1}),1.0]])]});}
            var Q26;
            {var subQ0=sQuery(id+"F0.wireOp",EDGE,"E34.MirrorC");var subQ1=sQuery(id+"F0.wireOp",EDGE,"E20.MirrorC");var subQ2=makeQuery(id+"F0.imprint","INTERSECT",VERTEX,{"disambiguationData":[OD(0.0)],"derivedFrom":[subQ1,subQ0]});Q26=makeQuery(id+"F0.imprint","IMPRINT",FACE,{"disambiguationData":[TD([[makeQuery(id+"F0.imprint","IMPRINT",EDGE,{"disambiguationData":[TD([[subQ2,-1.0]])],"derivedFrom":subQ1}),1.0]])]});}
            var Q27;
            Q27=makeQuery(id+"F0.imprint","IMPRINT",FACE,{"disambiguationData":[TD([[makeQuery(id+"F0.imprint","IMPRINT",EDGE,{"derivedFrom":sQuery(id+"F0.wireOp",EDGE,"E0")}),-1.0]])]});
            var Q28;
            {var subQ0=sQuery(id+"F0.wireOp",EDGE,"E4.3.0");var subQ1=sQuery(id+"F0.wireOp",EDGE,"E1");var subQ2=makeQuery(id+"F0.imprint","INTERSECT",VERTEX,{"disambiguationData":[OD(0.0)],"derivedFrom":[subQ1,subQ0]});Q28=makeQuery(id+"F0.imprint","IMPRINT",FACE,{"disambiguationData":[TD([[makeQuery(id+"F0.imprint","IMPRINT",EDGE,{"disambiguationData":[TD([[subQ2,1.0]])],"derivedFrom":subQ1}),1.0]])]});}
            var Q29;
            {var subQ0=sQuery(id+"F0.wireOp",EDGE,"E4.3.0");var subQ1=sQuery(id+"F0.wireOp",EDGE,"E1");var subQ2=makeQuery(id+"F0.imprint","INTERSECT",VERTEX,{"disambiguationData":[OD(0.0)],"derivedFrom":[subQ1,subQ0]});Q29=makeQuery(id+"F0.imprint","IMPRINT",FACE,{"disambiguationData":[TD([[makeQuery(id+"F0.imprint","IMPRINT",EDGE,{"disambiguationData":[TD([[subQ2,1.0]])],"derivedFrom":subQ1}),-1.0]])]});}
            var Q30;
            {var subQ0=sQuery(id+"F0.wireOp",EDGE,"E6");var subQ1=sQuery(id+"F0.wireOp",EDGE,"E1");var subQ2=makeQuery(id+"F0.imprint","INTERSECT",VERTEX,{"disambiguationData":[OD(0.0)],"derivedFrom":[subQ1,subQ0]});Q30=makeQuery(id+"F0.imprint","IMPRINT",FACE,{"disambiguationData":[TD([[makeQuery(id+"F0.imprint","IMPRINT",EDGE,{"disambiguationData":[TD([[subQ2,-1.0]])],"derivedFrom":subQ1}),1.0]])]});}
            var Q31;
            {var subQ0=sQuery(id+"F0.wireOp",EDGE,"E6");var subQ1=sQuery(id+"F0.wireOp",EDGE,"E1");var subQ2=makeQuery(id+"F0.imprint","INTERSECT",VERTEX,{"disambiguationData":[OD(0.0)],"derivedFrom":[subQ1,subQ0]});Q31=makeQuery(id+"F0.imprint","IMPRINT",FACE,{"disambiguationData":[TD([[makeQuery(id+"F0.imprint","IMPRINT",EDGE,{"disambiguationData":[TD([[subQ2,-1.0]])],"derivedFrom":subQ1}),-1.0]])]});}
            var Q32;
            {var subQ0=sQuery(id+"F0.wireOp",EDGE,"E9");var subQ1=sQuery(id+"F0.wireOp",EDGE,"E1");var subQ2=makeQuery(id+"F0.imprint","INTERSECT",VERTEX,{"disambiguationData":[OD(0.0)],"derivedFrom":[subQ1,subQ0]});Q32=makeQuery(id+"F0.imprint","IMPRINT",FACE,{"disambiguationData":[TD([[makeQuery(id+"F0.imprint","IMPRINT",EDGE,{"disambiguationData":[TD([[subQ2,-1.0]])],"derivedFrom":subQ1}),-1.0]])]});}
            var Q33;
            {var subQ0=sQuery(id+"F0.wireOp",EDGE,"E9");var subQ1=sQuery(id+"F0.wireOp",EDGE,"E1");var subQ2=makeQuery(id+"F0.imprint","INTERSECT",VERTEX,{"disambiguationData":[OD(0.0)],"derivedFrom":[subQ1,subQ0]});Q33=makeQuery(id+"F0.imprint","IMPRINT",FACE,{"disambiguationData":[TD([[makeQuery(id+"F0.imprint","IMPRINT",EDGE,{"disambiguationData":[TD([[subQ2,-1.0]])],"derivedFrom":subQ1}),1.0]])]});}
            var Q34;
            {var subQ0=sQuery(id+"F0.wireOp",EDGE,"E8");var subQ1=sQuery(id+"F0.wireOp",EDGE,"E1");var subQ2=makeQuery(id+"F0.imprint","INTERSECT",VERTEX,{"disambiguationData":[OD(0.0)],"derivedFrom":[subQ1,subQ0]});Q34=makeQuery(id+"F0.imprint","IMPRINT",FACE,{"disambiguationData":[TD([[makeQuery(id+"F0.imprint","IMPRINT",EDGE,{"disambiguationData":[TD([[subQ2,-1.0]])],"derivedFrom":subQ1}),1.0]])]});}
            var Q35;
            {var subQ0=sQuery(id+"F0.wireOp",EDGE,"E8");var subQ1=sQuery(id+"F0.wireOp",EDGE,"E1");var subQ2=makeQuery(id+"F0.imprint","INTERSECT",VERTEX,{"disambiguationData":[OD(0.0)],"derivedFrom":[subQ1,subQ0]});Q35=makeQuery(id+"F0.imprint","IMPRINT",FACE,{"disambiguationData":[TD([[makeQuery(id+"F0.imprint","IMPRINT",EDGE,{"disambiguationData":[TD([[subQ2,-1.0]])],"derivedFrom":subQ1}),-1.0]])]});}
            extrude(context, id + "F3", {"entities" : qUnion([Q0, Q1, Q2, Q3, Q4, Q5, Q6, Q7, Q8, Q9, Q10, Q11, Q12, Q13, Q14, Q15, Q16, Q17, Q18, Q19, Q20, Q21, Q22, Q23, Q24, Q25, Q26, Q27, Q28, Q29, Q30, Q31, Q32, Q33, Q34, Q35]), "depth" : 30 * mm});
        }
        {
            var Q0;
            Q0=makeQuery(id+"F0.imprint","IMPRINT",FACE,{"disambiguationData":[TD([[makeQuery(id+"F0.imprint","IMPRINT",EDGE,{"derivedFrom":sQuery(id+"F0.wireOp",EDGE,"E140.top")}),1.0]])]});
            var Q1;
            {var subQ4=sQuery(id+"F0.wireOp",EDGE,"E151.bottom");Q1=makeQuery(id+"F0.imprint","IMPRINT",FACE,{"disambiguationData":[TD([[makeQuery(id+"F0.imprint","IMPRINT",EDGE,{"derivedFrom":subQ4}),-1.0]])]});}
            extrude(context, id + "F4", {"entities" : qUnion([Q0, Q1]), "depth" : 5 * mm});
        }
    });
